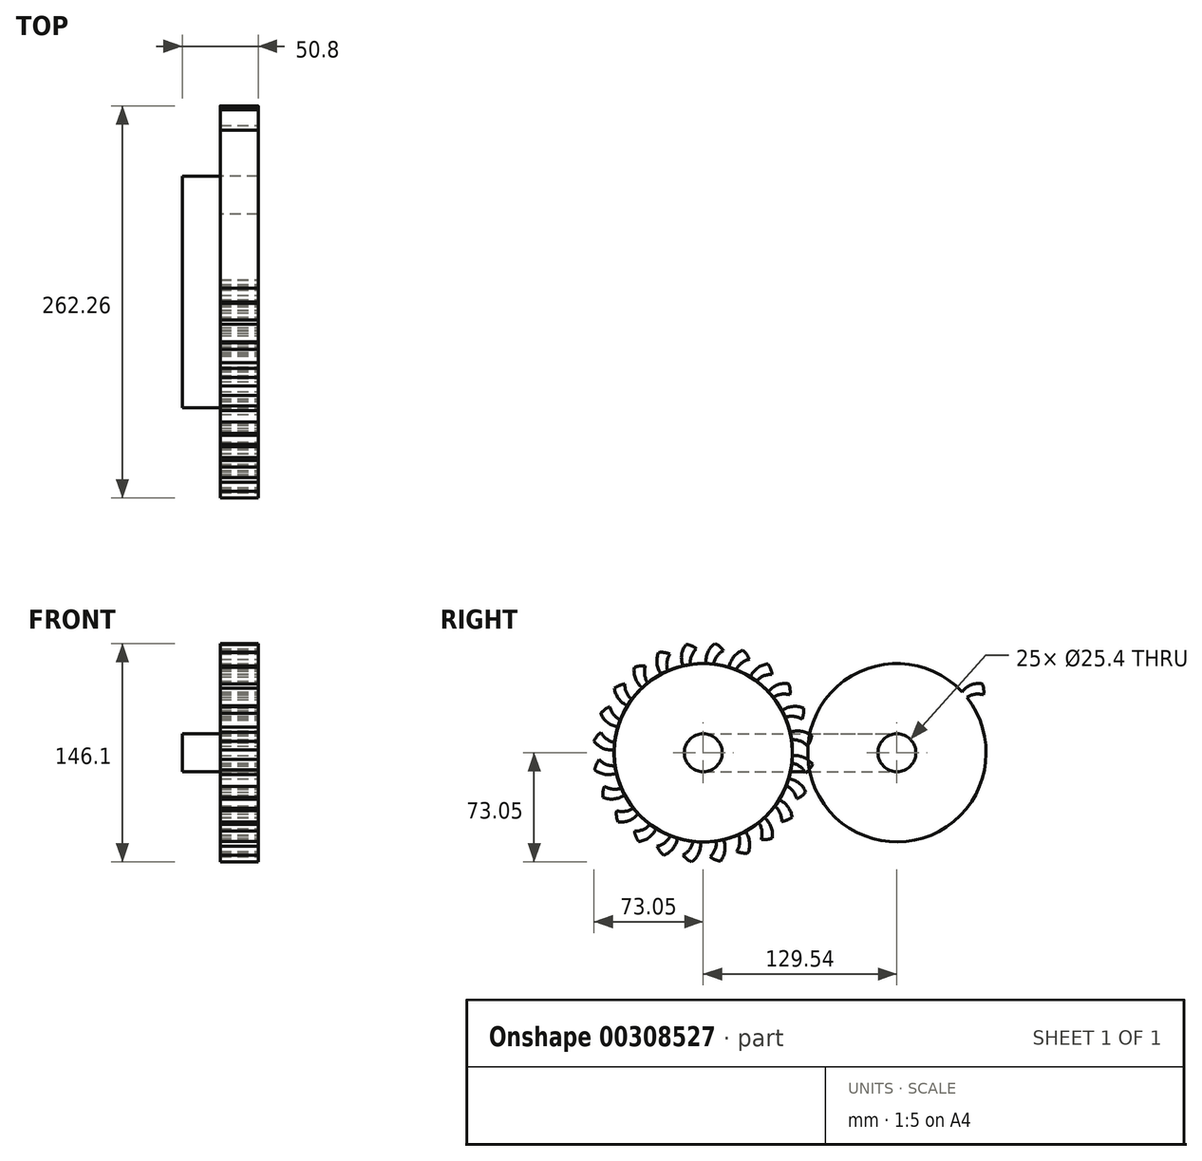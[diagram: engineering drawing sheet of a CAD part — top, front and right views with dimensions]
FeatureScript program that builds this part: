
annotation { "Feature Type Name" : "Feature", "Feature Type Description" : "" }
export const myFeature = defineFeature(function(context is Context, id is Id, definition is map)
    precondition{}
    {
        {
            var Q0;
            Q0=qCreatedBy(makeId("Right.planeOp"),FACE);
            var sketch = newSketch(context, id + "F0", { "sketchPlane" : qUnion([Q0])});
            skLineSegment(sketch, "E0.bottom", {"start": v(0, 0) * mm, "end": v(129.54, 0) * mm});
            skLineSegment(sketch, "E0.top", {"start": v(0, 25.4) * mm, "end": v(129.54, 25.4) * mm});
            skLineSegment(sketch, "E0.left", {"start": v(0, 0) * mm, "end": v(0, 25.4) * mm});
            skLineSegment(sketch, "E0.right", {"start": v(129.54, 0) * mm, "end": v(129.54, 25.4) * mm});
            skCircle(sketch, "E1", {"center": v(0, 12.7) * mm, "radius": 12.7 * mm});
            skCircle(sketch, "E2", {"center": v(129.54, 12.7) * mm, "radius": 12.7 * mm});
            skSolve(sketch);
        }
        {
            var Q0;
            {var subQ0=sQuery(id+"F0.wireOp",EDGE,"E0.left");Q0=makeQuery(id+"F0.imprint","IMPRINT",FACE,{"disambiguationData":[TD([[makeQuery(id+"F0.imprint","IMPRINT",EDGE,{"derivedFrom":subQ0}),1.0]])]});}
            var Q1;
            {var subQ0=sQuery(id+"F0.wireOp",EDGE,"E0.left");Q1=makeQuery(id+"F0.imprint","IMPRINT",FACE,{"disambiguationData":[TD([[makeQuery(id+"F0.imprint","IMPRINT",EDGE,{"derivedFrom":subQ0}),-1.0]])]});}
            var Q2;
            {var subQ0=sQuery(id+"F0.wireOp",EDGE,"E0.bottom");Q2=makeQuery(id+"F0.imprint","IMPRINT",FACE,{"disambiguationData":[TD([[makeQuery(id+"F0.imprint","IMPRINT",EDGE,{"derivedFrom":subQ0}),1.0]])]});}
            var Q3;
            {var subQ0=sQuery(id+"F0.wireOp",EDGE,"E0.right");Q3=makeQuery(id+"F0.imprint","IMPRINT",FACE,{"disambiguationData":[TD([[makeQuery(id+"F0.imprint","IMPRINT",EDGE,{"derivedFrom":subQ0}),1.0]])]});}
            var Q4;
            {var subQ0=sQuery(id+"F0.wireOp",EDGE,"E0.right");Q4=makeQuery(id+"F0.imprint","IMPRINT",FACE,{"disambiguationData":[TD([[makeQuery(id+"F0.imprint","IMPRINT",EDGE,{"derivedFrom":subQ0}),-1.0]])]});}
            extrude(context, id + "F1", {"entities" : qUnion([Q0, Q1, Q2, Q3, Q4]), "depth" : 25.4 * mm});
        }
        {
            var Q0;
            {var subQ0=sQuery(id+"F0.wireOp",EDGE,"E0.right");Q0=makeQuery(id+"F0.imprint","IMPRINT",FACE,{"disambiguationData":[TD([[makeQuery(id+"F0.imprint","IMPRINT",EDGE,{"derivedFrom":subQ0}),-1.0]])]});}
            var Q1;
            {var subQ0=sQuery(id+"F0.wireOp",EDGE,"E0.right");Q1=makeQuery(id+"F0.imprint","IMPRINT",FACE,{"disambiguationData":[TD([[makeQuery(id+"F0.imprint","IMPRINT",EDGE,{"derivedFrom":subQ0}),1.0]])]});}
            var Q2;
            {var subQ0=sQuery(id+"F0.wireOp",EDGE,"E0.left");Q2=makeQuery(id+"F0.imprint","IMPRINT",FACE,{"disambiguationData":[TD([[makeQuery(id+"F0.imprint","IMPRINT",EDGE,{"derivedFrom":subQ0}),-1.0]])]});}
            var Q3;
            {var subQ0=sQuery(id+"F0.wireOp",EDGE,"E0.left");Q3=makeQuery(id+"F0.imprint","IMPRINT",FACE,{"disambiguationData":[TD([[makeQuery(id+"F0.imprint","IMPRINT",EDGE,{"derivedFrom":subQ0}),1.0]])]});}
            extrude(context, id + "F2", {"entities" : qUnion([Q0, Q1, Q2, Q3]), "operationType" : NewBodyOperationType.ADD, "depth" : 50.8 * mm});
        }
        {
            var Q0;
            Q0=makeQuery(id+"F2.opExtrude","CAP_FACE",FACE,{"disambiguationData":[OSD([sQuery(id+"F0.wireOp",EDGE,"E1")])],"isStart":false});
            var sketch = newSketch(context, id + "F3", { "sketchPlane" : qUnion([Q0])});
            skCircle(sketch, "E3", {"center": v(0, 12.7) * mm, "radius": 12.7 * mm});
            skCircle(sketch, "E4", {"center": v(0, 12.7) * mm, "radius": 53.72 * mm, "construction": true});
            skCircle(sketch, "E5", {"center": v(0, 12.7) * mm, "radius": 58.67 * mm, "construction": true});
            skCircle(sketch, "E6", {"center": v(0, 12.7) * mm, "radius": 63.5 * mm, "construction": true});
            skLineSegment(sketch, "E7", {"start": v(0, 12.7) * mm, "end": v(0, 84.74) * mm, "construction": true});
            skLineSegment(sketch, "E8", {"start": v(0, 12.7) * mm, "end": v(-5.23, 92.56) * mm, "construction": true});
            skLineSegment(sketch, "E9", {"start": v(0, 76.2) * mm, "end": v(-50.89, 76.2) * mm, "construction": true});
            skLineSegment(sketch, "E10", {"start": v(0, 76.2) * mm, "end": v(-50.89, 57.68) * mm, "construction": true});
            skCircle(sketch, "E11", {"center": v(0, 12.7) * mm, "radius": 59.67 * mm});
            skCircle(sketch, "E12", {"center": v(0, 76.2) * mm, "radius": 14.6 * mm});
            skCircle(sketch, "E13", {"center": v(-13.57, 70.8) * mm, "radius": 14.6 * mm});
            skArc(sketch, "E14", {"start": v(0.95, 72.36) * mm, "mid": v(-0.68, 77.96) * mm, "end": v(-4.56, 82.3) * mm});
            skArc(sketch, "E15.MirrorCS", {"start": v(-8.73, 71.73) * mm, "mid": v(-7.85, 77.49) * mm, "end": v(-4.56, 82.3) * mm});
            skSolve(sketch);
        }
        {
            var Q0;
            Q0=makeQuery(id+"F3.imprint","IMPRINT",FACE,{"disambiguationData":[TD([[makeQuery(id+"F3.imprint","IMPRINT",EDGE,{"derivedFrom":sQuery(id+"F3.wireOp",EDGE,"E3")}),-1.0]])]});
            var Q1;
            {var subQ0=sQuery(id+"F3.wireOp",EDGE,"E13");var subQ1=sQuery(id+"F3.wireOp",EDGE,"E11");var subQ2=makeQuery(id+"F3.imprint","INTERSECT",VERTEX,{"derivedFrom":[subQ1,subQ0]});Q1=makeQuery(id+"F3.imprint","IMPRINT",FACE,{"disambiguationData":[TD([[makeQuery(id+"F3.imprint","IMPRINT",EDGE,{"disambiguationData":[TD([[subQ2,1.0]])],"derivedFrom":subQ1}),1.0]])]});}
            var Q2;
            {var subQ1=sQuery(id+"F3.wireOp",EDGE,"E11");var subQ3=makeQuery(id+"F3.imprint","INTERSECT",VERTEX,{"derivedFrom":[subQ1,sQuery(id+"F3.wireOp",EDGE,"E15.MirrorCS")]});Q2=makeQuery(id+"F3.imprint","IMPRINT",FACE,{"disambiguationData":[TD([[makeQuery(id+"F3.imprint","IMPRINT",EDGE,{"disambiguationData":[TD([[subQ3,-1.0]])],"derivedFrom":subQ1}),1.0]])]});}
            var Q3;
            {var subQ1=sQuery(id+"F3.wireOp",EDGE,"E11");var subQ3=sQuery(id+"F3.wireOp",EDGE,"E12");var subQ4=makeQuery(id+"F3.imprint","INTERSECT",VERTEX,{"disambiguationData":[OD(0.0)],"derivedFrom":[subQ1,subQ3]});Q3=makeQuery(id+"F3.imprint","IMPRINT",FACE,{"disambiguationData":[TD([[makeQuery(id+"F3.imprint","IMPRINT",EDGE,{"disambiguationData":[TD([[subQ4,1.0]])],"derivedFrom":subQ3}),1.0]])]});}
            var Q4;
            {var subQ4=sQuery(id+"F3.wireOp",EDGE,"E15.MirrorCS");Q4=makeQuery(id+"F3.imprint","IMPRINT",FACE,{"disambiguationData":[TD([[makeQuery(id+"F3.imprint","IMPRINT",EDGE,{"derivedFrom":subQ4}),-1.0]])]});}
            extrude(context, id + "F4", {"entities" : qUnion([Q0, Q1, Q2, Q3, Q4]), "oppositeDirection" : true, "depth" : 25.4 * mm});
        }
        {
            var Q0;
            Q0=makeQuery(id+"F4.opExtrude","SWEPT_BODY",BODY,{"disambiguationData":[OSD([sQuery(id+"F3.wireOp",EDGE,"E3"),sQuery(id+"F3.wireOp",EDGE,"E11"),sQuery(id+"F3.wireOp",EDGE,"E13"),sQuery(id+"F3.wireOp",EDGE,"E15.MirrorCS")])]});
            var Q1;
            Q1=makeQuery(id+"F4.opExtrude","SWEPT_FACE",FACE,{"disambiguationData":[OSD([sQuery(id+"F3.wireOp",EDGE,"E11")])]});
            circularPattern(context, id + "F5", {"entities" : qUnion([Q0]), "axis" : qUnion([Q1]), "angle" : 15 * degree, "instanceCount" : 24, "oppositeDirection" : true});
        }
        {
            var Q0;
            Q0=makeQuery(id+"F5.opPattern","COPY",BODY,{"derivedFrom":makeQuery(id+"F4.opExtrude","SWEPT_BODY",BODY,{"disambiguationData":[OSD([sQuery(id+"F3.wireOp",EDGE,"E3"),sQuery(id+"F3.wireOp",EDGE,"E11"),sQuery(id+"F3.wireOp",EDGE,"E13"),sQuery(id+"F3.wireOp",EDGE,"E15.MirrorCS")])]}),"instanceName":"4"});
            transform(context, id + "F6", {"entities" : qUnion([Q0]), "transformType" : TransformType.TRANSLATION_3D, "dx" : 0 * mm, "dy" : 129.54 * mm, "dz" : 0 * mm, "makeCopy" : true});
        }
    });
